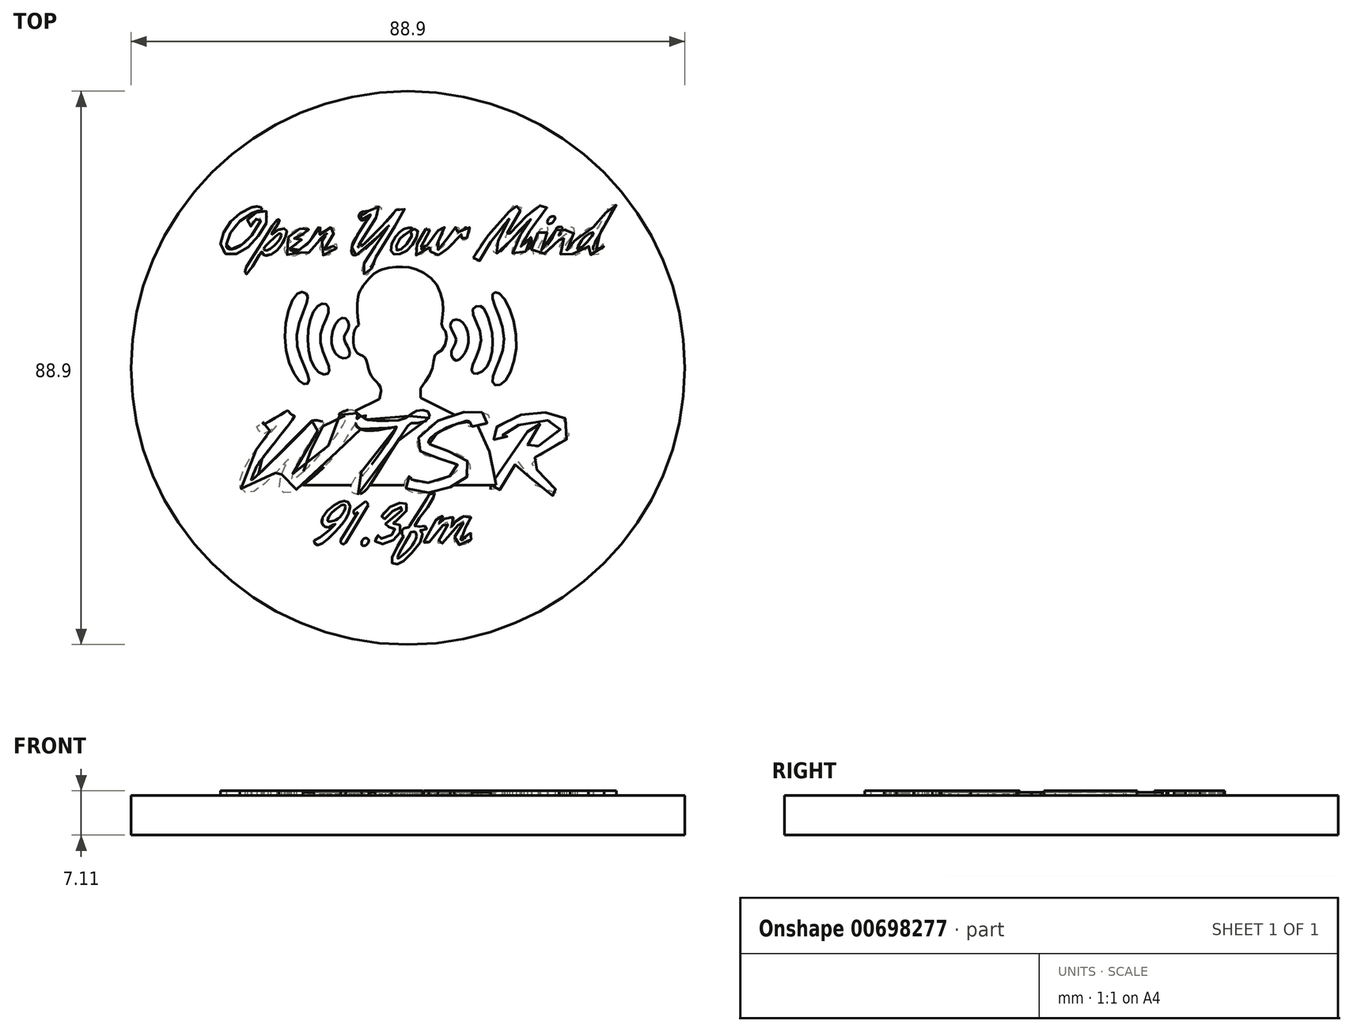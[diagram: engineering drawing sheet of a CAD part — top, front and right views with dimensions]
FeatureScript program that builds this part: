
annotation { "Feature Type Name" : "Feature", "Feature Type Description" : "" }
export const myFeature = defineFeature(function(context is Context, id is Id, definition is map)
    precondition{}
    {
        {
            var Q0;
            Q0=qCreatedBy(makeId("Top.planeOp"),FACE);
            var sketch = newSketch(context, id + "F0", { "sketchPlane" : qUnion([Q0])});
            skCircle(sketch, "E0", {"center": v(0, 0) * mm, "radius": 44.45 * mm});
            skSolve(sketch);
        }
        {
            var Q0;
            Q0 = qSketchRegion(id + "F0", true);
            extrude(context, id + "F1", {"entities" : qUnion([Q0]), "depth" : 6.35 * mm, "offsetDistance" : 25.4 * mm});
        }
        {
            var Q0;
            Q0=makeQuery(id+"F1.opExtrude","CAP_FACE",FACE,{"disambiguationData":[OSD([sQuery(id+"F0.wireOp",EDGE,"E0")])],"isStart":false});
            var sketch = newSketch(context, id + "F2", { "sketchPlane" : qUnion([Q0])});
            skFitSpline(sketch, "E1", {"points": [v(-1.88, 16.19) * mm, v(-4.9, 15.48) * mm, v(-6.9, 13.58) * mm, v(-8, 11.37) * mm, v(-7.9, 6.85) * mm], "startDerivative": vector(-13.7, -0.82) * mm, "endDerivative": vector(2.65, -16.75) * mm});
            skFitSpline(sketch, "E2", {"points": [v(-7.9, 6.85) * mm, v(-8.6, 5.95) * mm, v(-8.6, 3.24) * mm, v(-7.9, 2.24) * mm, v(-6.9, 1.64) * mm, v(-6.4, 0) * mm, v(-5.6, -1.68) * mm, v(-4.4, -3.18) * mm, v(-4.6, -4.99) * mm], "startDerivative": vector(-9.6, -5.75) * mm, "endDerivative": vector(-4.23, -14.62) * mm});
            skLineSegment(sketch, "E3", {"start": v(-4.6, -4.99) * mm, "end": v(-13.62, -9.4) * mm});
            skLineSegment(sketch, "E4", {"start": v(-13.62, -9.4) * mm, "end": v(-15.63, -13.32) * mm});
            skLineSegment(sketch, "E5", {"start": v(-15.63, -13.32) * mm, "end": v(-17.54, -18.84) * mm});
            skLineSegment(sketch, "E6", {"start": v(-17.54, -18.84) * mm, "end": v(14.17, -18.84) * mm});
            skLineSegment(sketch, "E7", {"start": v(14.17, -18.84) * mm, "end": v(13.07, -13.42) * mm});
            skLineSegment(sketch, "E8", {"start": v(13.07, -13.42) * mm, "end": v(11.26, -9.4) * mm});
            skLineSegment(sketch, "E9", {"start": v(11.26, -9.4) * mm, "end": v(2.03, -4.79) * mm});
            skLineSegment(sketch, "E10", {"start": v(2.03, -4.79) * mm, "end": v(2.03, -3.28) * mm});
            skFitSpline(sketch, "E11", {"points": [v(2.03, -3.28) * mm, v(3.94, 0) * mm, v(4.44, 2.24) * mm, v(5.44, 2.84) * mm, v(6.15, 5.65) * mm, v(5.44, 6.65) * mm, v(5.64, 9.06) * mm, v(4.44, 13.58) * mm, v(0.83, 15.98) * mm, v(-1.88, 16.19) * mm], "startDerivative": vector(18.22, 24.29) * mm, "endDerivative": vector(-22.07, -1.82) * mm});
            skSolve(sketch);
        }
        {
            var Q0;
            Q0=makeQuery(id+"F2.imprint","IMPRINT",FACE,{"disambiguationData":[TD([[makeQuery(id+"F2.imprint","IMPRINT",EDGE,{"derivedFrom":sQuery(id+"F2.wireOp",EDGE,"E1")}),-1.0]])]});
            var sketch = newSketch(context, id + "F3", { "sketchPlane" : qUnion([Q0])});
            skFitSpline(sketch, "E12", {"points": [v(-14.5, 9.93) * mm, v(-16.09, 4.37) * mm, v(-14.37, -0.67) * mm, v(-12.88, -0.95) * mm, v(-12.64, 0) * mm, v(-14.08, 4.63) * mm, v(-12.78, 8.87) * mm, v(-13.13, 10.23) * mm, v(-14.5, 9.93) * mm]});
            skFitSpline(sketch, "E13", {"points": [v(-12.28, 4.93) * mm, v(-10.92, 1.72) * mm, v(-9.47, 1.85) * mm, v(-9.6, 3.3) * mm, v(-10.26, 4.9) * mm, v(-9.47, 6.75) * mm, v(-10.42, 8.08) * mm, v(-12.28, 4.93) * mm]});
            skFitSpline(sketch, "E14", {"points": [v(6.82, 6.75) * mm, v(7.3, 7.65) * mm, v(8.5, 7.54) * mm, v(9.73, 5.03) * mm, v(9.07, 2.25) * mm, v(7.66, 1.2) * mm, v(6.93, 2.5) * mm, v(7.75, 4.37) * mm, v(6.82, 6.75) * mm]});
            skFitSpline(sketch, "E15", {"points": [v(10.4, 9.4) * mm, v(11.72, 4.9) * mm, v(10.26, 0) * mm, v(10.66, -0.93) * mm, v(12.51, 0) * mm, v(13.54, 5.15) * mm, v(12.45, 9) * mm, v(11.58, 9.93) * mm, v(10.4, 9.4) * mm]});
            skFitSpline(sketch, "E16", {"points": [v(13.57, 11.12) * mm, v(15.44, 4.64) * mm, v(13.7, -1.2) * mm, v(13.84, -2.65) * mm, v(15.3, -2.38) * mm, v(17.38, 5.05) * mm, v(14.63, 12) * mm, v(13.75, 12) * mm, v(13.57, 11.12) * mm]});
            skFitSpline(sketch, "E17", {"points": [v(-17.8, 11.92) * mm, v(-19.74, 4.06) * mm, v(-17.07, -2.42) * mm, v(-16.09, -2.52) * mm, v(-16.09, -1.06) * mm, v(-17.9, 4.9) * mm, v(-16.09, 11.25) * mm, v(-16.56, 12.06) * mm, v(-17.8, 11.92) * mm]});
            skSolve(sketch);
        }
        {
            var Q0;
            Q0=makeQuery(id+"F2.imprint","IMPRINT",FACE,{"disambiguationData":[TD([[makeQuery(id+"F2.imprint","IMPRINT",EDGE,{"derivedFrom":sQuery(id+"F2.wireOp",EDGE,"E1")}),-1.0]])]});
            var sketch = newSketch(context, id + "F4", { "sketchPlane" : qUnion([Q0])});
            skFitSpline(sketch, "E18", {"points": [v(-25.1, 25.78) * mm, v(-26.76, 24.97) * mm, v(-28.16, 23.84) * mm, v(-29.4, 22.12) * mm, v(-29.95, 20.83) * mm, v(-30, 19.04) * mm, v(-28.9, 18.2) * mm, v(-27.6, 18.33) * mm, v(-25.69, 19.37) * mm, v(-23.92, 21.3) * mm, v(-22.62, 23.54) * mm, v(-22.67, 25.11) * mm, v(-23.44, 25.23) * mm, v(-25.15, 24.5) * mm, v(-25.8, 23.5) * mm, v(-25.25, 22.67) * mm, v(-25.22, 23.04) * mm, v(-24.54, 23.81) * mm, v(-23.56, 24.19) * mm, v(-24.42, 22.19) * mm, v(-26.06, 20.31) * mm, v(-27.45, 19.32) * mm, v(-28.79, 19.1) * mm, v(-29.14, 19.54) * mm, v(-28.99, 20.6) * mm, v(-27.82, 22.68) * mm, v(-25.94, 24.4) * mm, v(-24.22, 25.16) * mm, v(-23.6, 25.29) * mm], "startDerivative": vector(-48.02, -21.2) * mm, "endDerivative": vector(24.02, 3.65) * mm});
            skLineSegment(sketch, "E19", {"start": v(-23.6, 25.29) * mm, "end": v(-23.44, 25.7) * mm});
            skFitSpline(sketch, "E20", {"points": [v(-23.44, 25.7) * mm, v(-24.07, 25.9) * mm, v(-25.1, 25.78) * mm], "startDerivative": vector(-1.28, 0.48) * mm, "endDerivative": vector(-2.08, -0.5) * mm});
            skFitSpline(sketch, "E21", {"points": [v(-21.02, 23.75) * mm, v(-23.7, 19.78) * mm, v(-26.13, 15.73) * mm, v(-26.13, 15.26) * mm, v(-25.9, 15.05) * mm, v(-23.45, 18.7) * mm, v(-23.35, 18.29) * mm, v(-22.08, 18.22) * mm, v(-20.35, 19.71) * mm, v(-19.43, 21.73) * mm, v(-19.59, 22.25) * mm, v(-20.62, 22.3) * mm, v(-22, 21.33) * mm, v(-20.79, 23.24) * mm, v(-20.7, 23.82) * mm, v(-21.02, 23.75) * mm]});
            skFitSpline(sketch, "E22", {"points": [v(-23.14, 19.12) * mm, v(-22.25, 20.15) * mm, v(-20.68, 21.56) * mm, v(-20.39, 21.54) * mm, v(-20.37, 21.16) * mm, v(-21.19, 19.9) * mm, v(-22.32, 19) * mm, v(-22.84, 18.86) * mm, v(-23.14, 19.12) * mm]});
            skFitSpline(sketch, "E23", {"points": [v(-17.34, 22.4) * mm, v(-18.7, 21.68) * mm, v(-19.14, 20.73) * mm, v(-18.73, 20.2) * mm, v(-19.28, 19.99) * mm, v(-19.9, 19.04) * mm, v(-19.12, 18.05) * mm, v(-17.4, 18.32) * mm, v(-16.76, 18.6) * mm, v(-16.62, 18.35) * mm, v(-16.2, 18.3) * mm, v(-14.65, 20.07) * mm, v(-13.02, 21.57) * mm, v(-13.99, 19.85) * mm, v(-13.99, 18.35) * mm, v(-13.02, 18.1) * mm, v(-11.5, 19.18) * mm, v(-11.41, 19.82) * mm, v(-11.7, 19.93) * mm, v(-12.05, 19.43) * mm, v(-13, 18.82) * mm, v(-13.38, 19.02) * mm, v(-12.3, 21.01) * mm, v(-11.72, 22.04) * mm, v(-11.88, 22.43) * mm, v(-12.41, 22.54) * mm, v(-13.44, 22.04) * mm, v(-14.16, 21.4) * mm, v(-13.71, 22.31) * mm, v(-13.96, 22.5) * mm, v(-14.38, 22.48) * mm, v(-15.93, 20.13) * mm, v(-16.93, 19.35) * mm, v(-17.81, 18.8) * mm, v(-18.81, 18.88) * mm, v(-18.92, 19.21) * mm, v(-17.1, 20.35) * mm, v(-17.1, 20.65) * mm, v(-17.23, 20.82) * mm, v(-17.9, 20.76) * mm, v(-18.28, 20.82) * mm, v(-17.06, 21.73) * mm, v(-16.98, 21.4) * mm, v(-16.37, 21.46) * mm, v(-15.96, 22) * mm, v(-15.98, 22.4) * mm, v(-16.48, 22.48) * mm, v(-17.34, 22.4) * mm]});
            skSolve(sketch);
        }
        {
            var Q0;
            Q0=makeQuery(id+"F2.imprint","IMPRINT",FACE,{"disambiguationData":[TD([[makeQuery(id+"F2.imprint","IMPRINT",EDGE,{"derivedFrom":sQuery(id+"F2.wireOp",EDGE,"E1")}),-1.0]])]});
            var sketch = newSketch(context, id + "F5", { "sketchPlane" : qUnion([Q0])});
            skFitSpline(sketch, "E24", {"points": [v(-7.4, 25.07) * mm, v(-7.87, 24.5) * mm, v(-7.63, 23.79) * mm, v(-7.13, 23.73) * mm, v(-6.02, 24.6) * mm, v(-8.2, 21.22) * mm, v(-9, 19.49) * mm, v(-8.98, 18.3) * mm, v(-7.81, 18.35) * mm, v(-3.1, 22.83) * mm, v(-3.99, 21.46) * mm, v(-6.08, 18.32) * mm, v(-7.4, 16.05) * mm, v(-7.27, 15.3) * mm, v(-6.59, 14.95) * mm, v(-6.02, 15.72) * mm, v(-5.3, 16.65) * mm, v(-5.3, 16.86) * mm, v(-5.93, 16.26) * mm, v(-4.65, 18.62) * mm, v(-0.56, 25.31) * mm, v(-0.56, 25.5) * mm, v(-1.63, 25.52) * mm, v(-1.87, 25.46) * mm, v(-2.1, 25.07) * mm, v(-6.29, 20.62) * mm, v(-7.78, 19.4) * mm, v(-8, 19.43) * mm, v(-7.93, 19.7) * mm, v(-4.26, 25.5) * mm, v(-4.26, 25.7) * mm, v(-4.95, 25.97) * mm, v(-5.21, 25.97) * mm, v(-6.83, 24.83) * mm, v(-7.24, 24.69) * mm, v(-7.4, 25.07) * mm]});
            skFitSpline(sketch, "E25", {"points": [v(-1.24, 21.88) * mm, v(-2.4, 20.41) * mm, v(-2.68, 18.68) * mm, v(-2.05, 18.23) * mm, v(-0.47, 18.62) * mm, v(1.12, 20.47) * mm, v(1.56, 22.06) * mm, v(0.94, 22.3) * mm, v(0.43, 22) * mm, v(0.37, 21.6) * mm, v(0.7, 21.6) * mm, v(-0.4, 19.67) * mm, v(-1.54, 18.89) * mm, v(-1.9, 19.04) * mm, v(-1.36, 20.65) * mm, v(0.13, 21.82) * mm, v(0.67, 22.44) * mm, v(-0.35, 22.41) * mm, v(-1.24, 21.88) * mm]});
            skFitSpline(sketch, "E26", {"points": [v(2.88, 22.3) * mm, v(1.39, 19.73) * mm, v(1.18, 18.3) * mm, v(1.74, 18.08) * mm, v(3.74, 19.55) * mm, v(3.74, 19.4) * mm, v(3.66, 18.6) * mm, v(4.1, 18.08) * mm, v(5.12, 18.3) * mm, v(5.33, 18.65) * mm, v(5.36, 18.6) * mm, v(5.3, 18.35) * mm, v(5.69, 18.35) * mm, v(6.88, 19.79) * mm, v(8.91, 21.67) * mm, v(8.91, 21.58) * mm, v(8.61, 20.83) * mm, v(8.8, 20.53) * mm, v(9.1, 20.5) * mm, v(10.08, 22.06) * mm, v(9.84, 22.6) * mm, v(8.34, 22.03) * mm, v(7.72, 21.34) * mm, v(7.63, 21.34) * mm, v(8.22, 22.3) * mm, v(8.1, 22.5) * mm, v(7.66, 22.6) * mm, v(7.09, 22.09) * mm, v(5.48, 19.4) * mm, v(4.61, 18.95) * mm, v(4.46, 19.22) * mm, v(5.84, 22.3) * mm, v(5.84, 22.6) * mm, v(5.12, 22.38) * mm, v(4.97, 22.27) * mm, v(3.24, 19.85) * mm, v(2.25, 19.1) * mm, v(2.07, 19.25) * mm, v(3.45, 21.94) * mm, v(3.54, 22.27) * mm, v(3.33, 22.33) * mm, v(2.88, 22.3) * mm]});
            skFitSpline(sketch, "E27", {"points": [v(10.48, 17.66) * mm, v(14, 22.6) * mm, v(16.85, 25.9) * mm, v(17, 26.09) * mm, v(17.51, 25.97) * mm, v(17.98, 25.93) * mm, v(18.2, 25.74) * mm, v(17.47, 24.35) * mm, v(15.54, 20.71) * mm, v(16.08, 21.3) * mm, v(18.83, 24.12) * mm, v(20.95, 26.09) * mm, v(21.42, 26.01) * mm, v(22.15, 25.93) * mm, v(22.34, 25.9) * mm, v(19.52, 21.95) * mm, v(18.01, 19.48) * mm, v(19.56, 20.56) * mm, v(19.71, 20.99) * mm, v(19.83, 19.9) * mm, v(17.86, 18.16) * mm, v(16.9, 18.28) * mm, v(16.93, 19.52) * mm, v(19.6, 23.5) * mm, v(19.75, 23.89) * mm, v(15.54, 19.4) * mm, v(14.34, 18.4) * mm, v(13.88, 18.51) * mm, v(13.8, 18.9) * mm, v(16.31, 23.92) * mm, v(13.07, 19.9) * mm, v(11.52, 17.24) * mm, v(11.25, 17.12) * mm, v(10.79, 17.31) * mm, v(10.48, 17.66) * mm]});
            skFitSpline(sketch, "E28", {"points": [v(20.87, 21.72) * mm, v(21.03, 21.33) * mm, v(19.83, 19.05) * mm, v(20.3, 18.24) * mm, v(21.88, 18.4) * mm, v(22.03, 18.2) * mm, v(23.7, 19.9) * mm, v(25.44, 21.6) * mm, v(25.4, 21.3) * mm, v(24.47, 19.9) * mm, v(24.31, 18.63) * mm, v(24.9, 18.09) * mm, v(26.36, 18.59) * mm, v(26.44, 18.36) * mm, v(27.56, 18.28) * mm, v(29.07, 19.55) * mm, v(29.03, 19.25) * mm, v(28.95, 18.63) * mm, v(29.22, 18.2) * mm, v(30.62, 18.36) * mm, v(31.43, 19.4) * mm, v(31.43, 19.9) * mm, v(31.27, 19.9) * mm, v(30.5, 19.13) * mm, v(29.76, 19.01) * mm, v(30.11, 20.25) * mm, v(33.36, 26.01) * mm, v(33.44, 26.2) * mm, v(32.74, 26.13) * mm, v(32.35, 25.97) * mm, v(30.23, 22.22) * mm, v(29.92, 22.6) * mm, v(27.83, 21.57) * mm, v(26.44, 19.9) * mm, v(26.4, 19.48) * mm, v(25.6, 18.9) * mm, v(25.09, 19.17) * mm, v(26.71, 21.8) * mm, v(26.52, 22.6) * mm, v(25.28, 22.3) * mm, v(24.24, 21.26) * mm, v(24.31, 21.53) * mm, v(24.7, 22.3) * mm, v(24.74, 22.6) * mm, v(24.04, 22.6) * mm, v(23.7, 22) * mm, v(21.88, 19.2) * mm, v(20.87, 18.94) * mm, v(22.5, 22.26) * mm, v(22.07, 22.6) * mm, v(20.87, 21.72) * mm]});
            skFitSpline(sketch, "E29", {"points": [v(22.61, 24) * mm, v(22.38, 23.5) * mm, v(22.54, 23.11) * mm, v(23.39, 23.54) * mm, v(23.58, 24.27) * mm, v(23.04, 24.31) * mm, v(22.61, 24) * mm]});
            skFitSpline(sketch, "E30", {"points": [v(27.48, 19.83) * mm, v(28.6, 21.22) * mm, v(29.73, 21.72) * mm, v(29.38, 20.99) * mm, v(27.99, 19.48) * mm, v(27.21, 19.05) * mm, v(27.48, 19.83) * mm]});
            skSolve(sketch);
        }
        {
            var Q0;
            Q0 = qSketchRegion(id + "F5", true);
            var Q1;
            Q1 = qSketchRegion(id + "F4", true);
            extrude(context, id + "F6", {"entities" : qUnion([Q0, Q1]), "operationType" : NewBodyOperationType.ADD, "depth" : 0.76 * mm, "offsetDistance" : 25.4 * mm});
        }
        {
            var Q0;
            Q0 = qSketchRegion(id + "F3", true);
            extrude(context, id + "F7", {"entities" : qUnion([Q0]), "operationType" : NewBodyOperationType.ADD, "depth" : 0.76 * mm, "offsetDistance" : 25.4 * mm});
        }
        {
            var Q0;
            Q0=makeQuery(id+"F2.imprint","IMPRINT",FACE,{"disambiguationData":[TD([[makeQuery(id+"F2.imprint","IMPRINT",EDGE,{"derivedFrom":sQuery(id+"F2.wireOp",EDGE,"E1")}),-1.0]])]});
            var sketch = newSketch(context, id + "F8", { "sketchPlane" : qUnion([Q0])});
            skFitSpline(sketch, "E31", {"points": [v(-23.36, -8.73) * mm, v(-23.22, -8.68) * mm, v(-23.3, -8.92) * mm, v(-23.19, -9.02) * mm, v(-19.75, -7.1) * mm, v(-19.52, -6.97) * mm, v(-19.35, -6.9) * mm, v(-18.93, -7.25) * mm, v(-18.35, -7.68) * mm, v(-18.22, -7.73) * mm, v(-21.23, -11.78) * mm, v(-23.44, -14.62) * mm], "startDerivative": vector(5.32, 2.81) * mm, "endDerivative": vector(-9.66, -12.63) * mm});
            skFitSpline(sketch, "E32", {"points": [v(-23.44, -14.62) * mm, v(-24.29, -15.85) * mm, v(-25.1, -17.8) * mm, v(-25.1, -18) * mm, v(-15.93, -9.13) * mm, v(-15.48, -8.57) * mm, v(-15.22, -8.4) * mm, v(-13.81, -8.57) * mm, v(-13.62, -8.67) * mm, v(-13.58, -8.96) * mm, v(-14, -9.52) * mm, v(-17.1, -14.05) * mm, v(-18.41, -16.73) * mm, v(-18.64, -17.55) * mm, v(-18.55, -17.87) * mm, v(-11.6, -10.99) * mm, v(-10.03, -7.72) * mm, v(-10.35, -7.56) * mm, v(-10.81, -7.56) * mm, v(-11.07, -7.5) * mm, v(-10.97, -7.33) * mm, v(-9.18, -6.71) * mm, v(-8.56, -6.87) * mm, v(-8.2, -7) * mm, v(-8.17, -8.21) * mm, v(-7.65, -7.83) * mm, v(-6.73, -7.68) * mm, v(-6.84, -7.99) * mm, v(-6.84, -8.26) * mm, v(-3.28, -8.5) * mm, v(-0.26, -8.03) * mm, v(1.13, -6.98) * mm, v(2.72, -6.83) * mm, v(3.41, -7.25) * mm, v(3.1, -8.38) * mm, v(0.67, -8.92) * mm, v(0.24, -9) * mm, v(-5.8, -18.36) * mm, v(-7.8, -20.26) * mm, v(-9.05, -19.9) * mm, v(-8.85, -18.32) * mm, v(-7.54, -16.7) * mm, v(-7.54, -16.97) * mm, v(-7.38, -17.28) * mm, v(-1.8, -9.47) * mm, v(-1.9, -9.47) * mm, v(-2.86, -9.65) * mm, v(-6.84, -10.04) * mm, v(-8.35, -9.15) * mm, v(-8.35, -8.8) * mm, v(-11.3, -13.37) * mm, v(-15.12, -17.43) * mm, v(-18.84, -20.03) * mm, v(-20.23, -19.9) * mm, v(-20.7, -18.86) * mm, v(-19.65, -15.7) * mm, v(-19.15, -14.62) * mm, v(-19.7, -15.19) * mm, v(-23.44, -18.98) * mm, v(-25.88, -20.06) * mm, v(-26.85, -19.33) * mm, v(-26.93, -17.94) * mm, v(-25.42, -14.62) * mm, v(-21.59, -9.92) * mm, v(-21.08, -9.3) * mm, v(-22.2, -10.16) * mm, v(-23.75, -10.58) * mm, v(-24.1, -9.73) * mm, v(-24.26, -9.5) * mm, v(-23.3, -8.7) * mm, v(-23.36, -8.73) * mm], "startDerivative": vector(-61.97, -76.51) * mm, "endDerivative": vector(-37.33, -21.68) * mm});
            skFitSpline(sketch, "E33", {"points": [v(1.7, -11.19) * mm, v(5.15, -8.33) * mm, v(9.5, -7.02) * mm, v(11.59, -7.12) * mm, v(12.94, -7.75) * mm, v(12.56, -9.01) * mm, v(11.54, -9.3) * mm, v(9.6, -9.35) * mm, v(9.49, -9.09) * mm, v(9.83, -8.69) * mm, v(9.9, -8.49) * mm, v(8.43, -8.8) * mm, v(6.07, -9.7) * mm, v(3.61, -11.3) * mm, v(3.35, -12.09) * mm, v(5.17, -13.01) * mm, v(8.55, -14.08) * mm, v(9.95, -15.82) * mm, v(9.4, -17.58) * mm, v(7.27, -18.95) * mm, v(4.69, -19.79) * mm, v(0.4, -19.88) * mm, v(-0.57, -18.43) * mm, v(0.08, -17.5) * mm, v(0.46, -17.27) * mm, v(0.63, -17.24) * mm, v(0.5, -17.66) * mm, v(1.08, -18.18) * mm, v(3.1, -18.43) * mm, v(6.43, -17.56) * mm, v(8.2, -15.98) * mm, v(7.75, -15.4) * mm, v(5.4, -14.66) * mm, v(2.37, -13.8) * mm, v(1.53, -12.25) * mm, v(1.7, -11.19) * mm]});
            skFitSpline(sketch, "E34", {"points": [v(13.54, -10.73) * mm, v(14.73, -9.01) * mm, v(18.62, -7.41) * mm, v(21.72, -7.16) * mm, v(24.15, -7.45) * mm, v(25.88, -9.01) * mm, v(25.1, -11.93) * mm, v(19.46, -14.56) * mm, v(19.21, -14.56) * mm, v(23.08, -19.08) * mm, v(23.7, -19.5) * mm, v(24.23, -19.25) * mm, v(23.61, -20.2) * mm, v(22.34, -20.56) * mm, v(17.73, -14.97) * mm, v(17.61, -14.89) * mm, v(14.94, -19.41) * mm, v(14.6, -19.62) * mm, v(13.62, -19.66) * mm, v(13.25, -19.29) * mm, v(20.08, -9.01) * mm, v(20.41, -8.7) * mm, v(21.2, -9.01) * mm, v(21.28, -9.3) * mm, v(18.73, -13.18) * mm, v(18.78, -13.36) * mm, v(23.27, -11.27) * mm, v(24.48, -9.66) * mm, v(23.88, -8.8) * mm, v(20.46, -8.48) * mm, v(16.32, -9.86) * mm, v(15.24, -10.77) * mm, v(15.2, -10.95) * mm, v(15.47, -10.99) * mm, v(15.84, -10.8) * mm, v(16.01, -10.85) * mm, v(15.3, -11.5) * mm, v(14.14, -11.73) * mm, v(13.62, -11.32) * mm, v(13.54, -10.73) * mm]});
            skSolve(sketch);
        }
        {
            var Q0;
            Q0=makeQuery(id+"F2.imprint","IMPRINT",FACE,{"disambiguationData":[TD([[makeQuery(id+"F2.imprint","IMPRINT",EDGE,{"derivedFrom":sQuery(id+"F2.wireOp",EDGE,"E1")}),-1.0]])]});
            var sketch = newSketch(context, id + "F9", { "sketchPlane" : qUnion([Q0])});
            skFitSpline(sketch, "E35", {"points": [v(-13.7, -24.06) * mm, v(-11.85, -22.03) * mm, v(-10.53, -21.41) * mm, v(-9.82, -21.41) * mm, v(-9.33, -21.94) * mm, v(-9.63, -23.65) * mm, v(-10.53, -25.02) * mm, v(-12.98, -27.6) * mm, v(-14.3, -28.45) * mm, v(-14.81, -28.39) * mm, v(-15.13, -27.8) * mm, v(-14.73, -27.62) * mm, v(-11.68, -25.12) * mm, v(-11.63, -25) * mm, v(-12.49, -25.57) * mm, v(-13.15, -25.57) * mm, v(-13.68, -25.19) * mm, v(-13.7, -24.06) * mm]});
            skFitSpline(sketch, "E36", {"points": [v(-12.87, -24.3) * mm, v(-11.85, -22.93) * mm, v(-10.55, -22.03) * mm, v(-10.2, -22.03) * mm, v(-10.04, -22.41) * mm, v(-11.04, -24.06) * mm, v(-12.15, -24.63) * mm, v(-12.83, -24.63) * mm, v(-12.87, -24.3) * mm]});
            skLineSegment(sketch, "E37", {"start": v(-8.03, -23.14) * mm, "end": v(-10.78, -27.66) * mm});
            skLineSegment(sketch, "E38", {"start": v(-6.37, -21.99) * mm, "end": v(-10, -28.04) * mm});
            skLineSegment(sketch, "E39", {"start": v(-8.7, -22.9) * mm, "end": v(-7.03, -21.62) * mm});
            skFitSpline(sketch, "E40", {"points": [v(-8.7, -22.9) * mm, v(-8.7, -23.33) * mm, v(-8.51, -23.5) * mm, v(-8.03, -23.14) * mm], "startDerivative": vector(-0.18, -1.35) * mm, "endDerivative": vector(1.31, 1.32) * mm});
            skFitSpline(sketch, "E41", {"points": [v(-7.03, -21.62) * mm, v(-6.77, -21.47) * mm, v(-6.37, -21.99) * mm], "startDerivative": vector(0.64, 0.62) * mm, "endDerivative": vector(0.68, -1.23) * mm});
            skFitSpline(sketch, "E42", {"points": [v(-10.78, -27.66) * mm, v(-10.78, -28.04) * mm, v(-10.32, -28.31) * mm, v(-10, -28.04) * mm], "startDerivative": vector(-0.33, -1.26) * mm, "endDerivative": vector(0.87, 1.18) * mm});
            skFitSpline(sketch, "E43", {"points": [v(-7.37, -27.8) * mm, v(-6.77, -27.34) * mm, v(-6.32, -27.66) * mm, v(-6.62, -28.4) * mm, v(-7.29, -28.54) * mm, v(-7.37, -27.8) * mm]});
            skFitSpline(sketch, "E44", {"points": [v(-4.27, -23.87) * mm, v(-2.43, -22.08) * mm, v(-1.2, -21.66) * mm, v(-0.4, -21.74) * mm, v(-0.17, -22.16) * mm, v(-0.35, -23.15) * mm, v(-2.28, -24.84) * mm, v(-2.5, -24.99) * mm, v(-1.88, -24.97) * mm, v(-1.31, -25.26) * mm, v(-1.14, -25.92) * mm, v(-1.74, -27.1) * mm, v(-3.17, -28.04) * mm, v(-4.84, -28.28) * mm, v(-5.3, -27.66) * mm, v(-4.88, -26.95) * mm, v(-4.73, -26.89) * mm, v(-4.58, -27.3) * mm, v(-3.17, -27.16) * mm, v(-2.03, -26.25) * mm, v(-2.1, -25.87) * mm, v(-2.56, -25.56) * mm, v(-3.4, -25.56) * mm, v(-3.6, -25.26) * mm, v(-3.57, -24.9) * mm, v(-3.3, -24.71) * mm, v(-0.93, -22.88) * mm, v(-0.77, -22.48) * mm, v(-1.2, -22.37) * mm, v(-2.47, -23.05) * mm, v(-3.7, -24.27) * mm, v(-3.97, -24.33) * mm, v(-4.27, -23.87) * mm]});
            skFitSpline(sketch, "E45", {"points": [v(-0.98, -26.3) * mm, v(-0.62, -25.76) * mm, v(0.05, -25.64) * mm, v(0.28, -25.4) * mm], "startDerivative": vector(0.7, 1.93) * mm, "endDerivative": vector(0.5, 1.53) * mm});
            skFitSpline(sketch, "E46", {"points": [v(0.28, -25.4) * mm, v(3.36, -20.44) * mm, v(3.48, -20.3) * mm, v(4.26, -20.17) * mm, v(4.3, -20.36) * mm, v(2.73, -23) * mm, v(1.12, -25.51) * mm, v(2.25, -25.43) * mm, v(2.7, -25.4) * mm, v(3.09, -25.8) * mm, v(2, -26.12) * mm, v(2.08, -26.16) * mm, v(2.33, -27.17) * mm, v(-0.3, -30.65) * mm, v(-1.75, -31.55) * mm, v(-2.5, -31.38) * mm, v(-2.5, -30.31) * mm, v(-0.62, -26.81) * mm, v(-0.62, -26.73) * mm, v(-1.1, -26.73) * mm, v(-0.98, -26.3) * mm, v(-0.9, -26.07) * mm], "startDerivative": vector(39.26, 60.45) * mm, "endDerivative": vector(2.12, 8.35) * mm});
            skFitSpline(sketch, "E47", {"points": [v(-1.67, -30.42) * mm, v(0.36, -26.58) * mm, v(0.4, -26.43) * mm, v(1.05, -26.33) * mm, v(1.24, -26.48) * mm, v(1.39, -26.96) * mm, v(0.53, -28.74) * mm, v(-0.69, -29.95) * mm, v(-1.57, -30.63) * mm, v(-1.67, -30.42) * mm]});
            skFitSpline(sketch, "E48", {"points": [v(4.68, -24.03) * mm, v(5.35, -23.75) * mm, v(5.56, -23.94) * mm, v(5, -25.07) * mm, v(4.97, -25.22) * mm, v(5.68, -24.49) * mm, v(6.98, -23.82) * mm, v(7.36, -23.98) * mm, v(7.38, -24.7) * mm, v(6.75, -25.8) * mm, v(8.22, -24.24) * mm, v(9.87, -23.75) * mm, v(10.15, -24.07) * mm, v(8.51, -26.96) * mm, v(8.43, -27.48) * mm, v(8.85, -27.6) * mm, v(10.12, -26.54) * mm, v(10.3, -26.58) * mm, v(10.33, -27.1) * mm, v(9.04, -28.36) * mm, v(7.74, -28.28) * mm, v(7.55, -26.94) * mm, v(9, -24.76) * mm, v(9, -24.63) * mm, v(6.94, -26.46) * mm, v(5.6, -28.15) * mm, v(5.01, -28.17) * mm, v(4.74, -27.99) * mm, v(5.85, -26.27) * mm, v(6.42, -24.86) * mm, v(6.35, -24.78) * mm, v(4.53, -26.48) * mm, v(3.34, -28.2) * mm, v(2.94, -28.22) * mm, v(2.58, -27.99) * mm, v(4.4, -24.57) * mm, v(4.68, -24.03) * mm]});
            skSolve(sketch);
        }
        {
            var Q0;
            {var subQ0=sQuery(id+"F8.wireOp",EDGE,"E32");var subQ8=makeQuery(id+"F2.imprint","IMPRINT",EDGE,{"derivedFrom":sQuery(id+"F2.wireOp",EDGE,"E5")});var subQ10=makeQuery(id+"F8.imprint","INTERSECT",VERTEX,{"derivedFrom":[subQ8,subQ0]});Q0=makeQuery(id+"F8.imprint","IMPRINT",FACE,{"disambiguationData":[TD([[makeQuery(id+"F8.imprint","IMPRINT",EDGE,{"disambiguationData":[TD([[subQ10,-1.0]])],"derivedFrom":subQ0}),-1.0]])]});}
            var Q1;
            {var subQ0=sQuery(id+"F8.wireOp",EDGE,"E32");var subQ1=makeQuery(id+"F2.imprint","IMPRINT",EDGE,{"derivedFrom":sQuery(id+"F2.wireOp",EDGE,"E3")});var subQ2=makeQuery(id+"F8.imprint","INTERSECT",VERTEX,{"disambiguationData":[OD(0.0)],"derivedFrom":[subQ1,subQ0]});Q1=makeQuery(id+"F8.imprint","IMPRINT",FACE,{"disambiguationData":[TD([[makeQuery(id+"F8.imprint","IMPRINT",EDGE,{"disambiguationData":[TD([[subQ2,-1.0]])],"derivedFrom":subQ0}),-1.0]])]});}
            var Q2;
            {var subQ3=sQuery(id+"F8.wireOp",EDGE,"E32");var subQ5=sQuery(id+"F8.wireOp",EDGE,"E31");var subQ8=makeQuery(id+"F8.imprint","INTERSECT",VERTEX,{"disambiguationData":[OD(1.0)],"derivedFrom":[subQ5,subQ3]});Q2=makeQuery(id+"F8.imprint","IMPRINT",FACE,{"disambiguationData":[TD([[makeQuery(id+"F8.imprint","IMPRINT",EDGE,{"disambiguationData":[TD([[subQ8,1.0]])],"derivedFrom":subQ5}),-1.0]])]});}
            var Q3;
            {var subQ0=sQuery(id+"F8.wireOp",EDGE,"E32");var subQ1=makeQuery(id+"F2.imprint","IMPRINT",EDGE,{"derivedFrom":sQuery(id+"F2.wireOp",EDGE,"E6")});var subQ2=makeQuery(id+"F8.imprint","INTERSECT",VERTEX,{"disambiguationData":[OD(0.0)],"derivedFrom":[subQ1,subQ0]});Q3=makeQuery(id+"F8.imprint","IMPRINT",FACE,{"disambiguationData":[TD([[makeQuery(id+"F8.imprint","IMPRINT",EDGE,{"disambiguationData":[TD([[subQ2,-1.0]])],"derivedFrom":subQ0}),-1.0]])]});}
            var Q4;
            {var subQ0=sQuery(id+"F8.wireOp",EDGE,"E33");var subQ1=makeQuery(id+"F2.imprint","IMPRINT",EDGE,{"derivedFrom":sQuery(id+"F2.wireOp",EDGE,"E6")});var subQ2=makeQuery(id+"F8.imprint","INTERSECT",VERTEX,{"disambiguationData":[OD(0.0)],"derivedFrom":[subQ1,subQ0]});Q4=makeQuery(id+"F8.imprint","IMPRINT",FACE,{"disambiguationData":[TD([[makeQuery(id+"F8.imprint","IMPRINT",EDGE,{"disambiguationData":[TD([[subQ2,-1.0]])],"derivedFrom":subQ0}),-1.0]])]});}
            var Q5;
            {var subQ0=sQuery(id+"F8.wireOp",EDGE,"E33");var subQ1=makeQuery(id+"F2.imprint","IMPRINT",EDGE,{"derivedFrom":sQuery(id+"F2.wireOp",EDGE,"E9")});var subQ2=makeQuery(id+"F8.imprint","INTERSECT",VERTEX,{"disambiguationData":[OD(3.0)],"derivedFrom":[subQ1,subQ0]});Q5=makeQuery(id+"F8.imprint","IMPRINT",FACE,{"disambiguationData":[TD([[makeQuery(id+"F8.imprint","IMPRINT",EDGE,{"disambiguationData":[TD([[subQ2,-1.0]])],"derivedFrom":subQ0}),-1.0]])]});}
            var Q6;
            {var subQ0=sQuery(id+"F8.wireOp",EDGE,"E33");var subQ1=makeQuery(id+"F2.imprint","IMPRINT",EDGE,{"derivedFrom":sQuery(id+"F2.wireOp",EDGE,"E9")});var subQ2=makeQuery(id+"F8.imprint","INTERSECT",VERTEX,{"disambiguationData":[OD(0.0)],"derivedFrom":[subQ1,subQ0]});Q6=makeQuery(id+"F8.imprint","IMPRINT",FACE,{"disambiguationData":[TD([[makeQuery(id+"F8.imprint","IMPRINT",EDGE,{"disambiguationData":[TD([[subQ2,1.0]])],"derivedFrom":subQ0}),-1.0]])]});}
            var Q7;
            {var subQ0=sQuery(id+"F8.wireOp",EDGE,"E33");var subQ1=makeQuery(id+"F2.imprint","IMPRINT",EDGE,{"derivedFrom":sQuery(id+"F2.wireOp",EDGE,"E9")});var subQ2=makeQuery(id+"F8.imprint","INTERSECT",VERTEX,{"disambiguationData":[OD(0.0)],"derivedFrom":[subQ1,subQ0]});Q7=makeQuery(id+"F8.imprint","IMPRINT",FACE,{"disambiguationData":[TD([[makeQuery(id+"F8.imprint","IMPRINT",EDGE,{"disambiguationData":[TD([[subQ2,-1.0]])],"derivedFrom":subQ0}),-1.0]])]});}
            var Q8;
            {var subQ0=sQuery(id+"F8.wireOp",EDGE,"E34");var subQ1=makeQuery(id+"F2.imprint","IMPRINT",EDGE,{"derivedFrom":sQuery(id+"F2.wireOp",EDGE,"E7")});var subQ2=makeQuery(id+"F8.imprint","INTERSECT",VERTEX,{"derivedFrom":[subQ1,subQ0]});Q8=makeQuery(id+"F8.imprint","IMPRINT",FACE,{"disambiguationData":[TD([[makeQuery(id+"F8.imprint","IMPRINT",EDGE,{"disambiguationData":[TD([[subQ2,-1.0]])],"derivedFrom":subQ0}),-1.0]])]});}
            extrude(context, id + "F10", {"entities" : qUnion([Q0, Q1, Q2, Q3, Q4, Q5, Q6, Q7, Q8]), "operationType" : NewBodyOperationType.ADD, "depth" : 0.76 * mm, "offsetDistance" : 25.4 * mm});
        }
        {
            var Q0;
            Q0=makeQuery(id+"F9.imprint","IMPRINT",FACE,{"disambiguationData":[TD([[makeQuery(id+"F9.imprint","IMPRINT",EDGE,{"derivedFrom":sQuery(id+"F9.wireOp",EDGE,"E35")}),-1.0]])]});
            var Q1;
            Q1=makeQuery(id+"F9.imprint","IMPRINT",FACE,{"disambiguationData":[TD([[makeQuery(id+"F9.imprint","IMPRINT",EDGE,{"derivedFrom":sQuery(id+"F9.wireOp",EDGE,"E37")}),1.0]])]});
            var Q2;
            Q2=makeQuery(id+"F9.imprint","IMPRINT",FACE,{"disambiguationData":[TD([[makeQuery(id+"F9.imprint","IMPRINT",EDGE,{"derivedFrom":sQuery(id+"F9.wireOp",EDGE,"E44")}),-1.0]])]});
            var Q3;
            Q3=makeQuery(id+"F9.imprint","IMPRINT",FACE,{"disambiguationData":[TD([[makeQuery(id+"F9.imprint","IMPRINT",EDGE,{"derivedFrom":sQuery(id+"F9.wireOp",EDGE,"E43")}),-1.0]])]});
            var Q4;
            Q4=makeQuery(id+"F9.imprint","IMPRINT",FACE,{"disambiguationData":[TD([[makeQuery(id+"F9.imprint","IMPRINT",EDGE,{"derivedFrom":sQuery(id+"F9.wireOp",EDGE,"E47")}),1.0]])]});
            extrude(context, id + "F11", {"entities" : qUnion([Q0, Q1, Q2, Q3, Q4]), "operationType" : NewBodyOperationType.ADD, "depth" : 0.76 * mm, "offsetDistance" : 25.4 * mm});
        }
        {
            var Q0;
            {var subQ7=sQuery(id+"F0.wireOp",EDGE,"E0");var subQ8=makeQuery(id+"F1.opExtrude","SWEPT_FACE",FACE,{"disambiguationData":[OSD([subQ7])]});Q0=makeQuery(id+"F11.boolean.opBoolean","SPLIT",FACE,{"disambiguationData":[TD([subQ8])],"derivedFrom":makeQuery(id+"F6.boolean.opBoolean","SPLIT",FACE,{"disambiguationData":[TD([subQ8])],"derivedFrom":makeQuery(id+"F1.opExtrude","CAP_FACE",FACE,{"disambiguationData":[OSD([subQ7])],"isStart":false})})});}
            var sketch = newSketch(context, id + "F12", { "sketchPlane" : qUnion([Q0])});
            skFitSpline(sketch, "E49", {"points": [v(2.56, -27.98) * mm, v(4.69, -24.07) * mm, v(4.76, -23.97) * mm, v(5.49, -23.78) * mm, v(5.57, -23.84) * mm, v(5.62, -23.97) * mm, v(5.46, -24.35) * mm, v(4.87, -25.14) * mm, v(4.83, -25.21) * mm, v(5.95, -24.23) * mm, v(6.81, -23.86) * mm, v(7.16, -23.91) * mm, v(7.37, -24.25) * mm, v(7.34, -24.77) * mm, v(6.86, -25.62) * mm, v(6.81, -25.75) * mm, v(7.65, -24.73) * mm, v(8.41, -24.1) * mm, v(9.16, -23.77) * mm, v(9.93, -23.73) * mm, v(10.08, -23.91) * mm, v(10.13, -24.34) * mm, v(9.76, -24.93) * mm, v(8.42, -27.18) * mm, v(8.5, -27.58) * mm, v(8.84, -27.59) * mm, v(10.07, -26.54) * mm, v(10.18, -26.52) * mm, v(10.26, -27.29) * mm, v(10.24, -27.42) * mm, v(9.16, -28.32) * mm, v(7.98, -28.36) * mm, v(7.5, -27.8) * mm, v(7.78, -26.54) * mm, v(8.91, -24.89) * mm, v(8.94, -24.82) * mm, v(8.96, -24.69) * mm, v(8.69, -24.72) * mm, v(5.57, -28.14) * mm, v(5.49, -28.27) * mm, v(4.9, -28.16) * mm, v(4.82, -28) * mm, v(6.18, -25.65) * mm, v(6.43, -24.87) * mm, v(6.29, -24.8) * mm, v(5.46, -25.43) * mm, v(3.36, -28.08) * mm, v(3.36, -28.16) * mm, v(2.72, -28.22) * mm, v(2.56, -27.98) * mm]});
            skSolve(sketch);
        }
        {
            var Q0;
            Q0=makeQuery(id+"F12.imprint","IMPRINT",FACE,{"disambiguationData":[TD([[makeQuery(id+"F12.imprint","IMPRINT",EDGE,{"derivedFrom":sQuery(id+"F12.wireOp",EDGE,"E49")}),-1.0]])]});
            extrude(context, id + "F13", {"entities" : qUnion([Q0]), "operationType" : NewBodyOperationType.ADD, "depth" : 0.76 * mm, "offsetDistance" : 25.4 * mm});
        }
        {
            var Q0;
            Q0=makeQuery(id+"F2.imprint","IMPRINT",FACE,{"disambiguationData":[TD([[makeQuery(id+"F2.imprint","IMPRINT",EDGE,{"derivedFrom":sQuery(id+"F2.wireOp",EDGE,"E1")}),1.0]])]});
            extrude(context, id + "F14", {"entities" : qUnion([Q0]), "operationType" : NewBodyOperationType.ADD, "depth" : 0.5 * mm, "offsetDistance" : 25.4 * mm});
        }
    });
